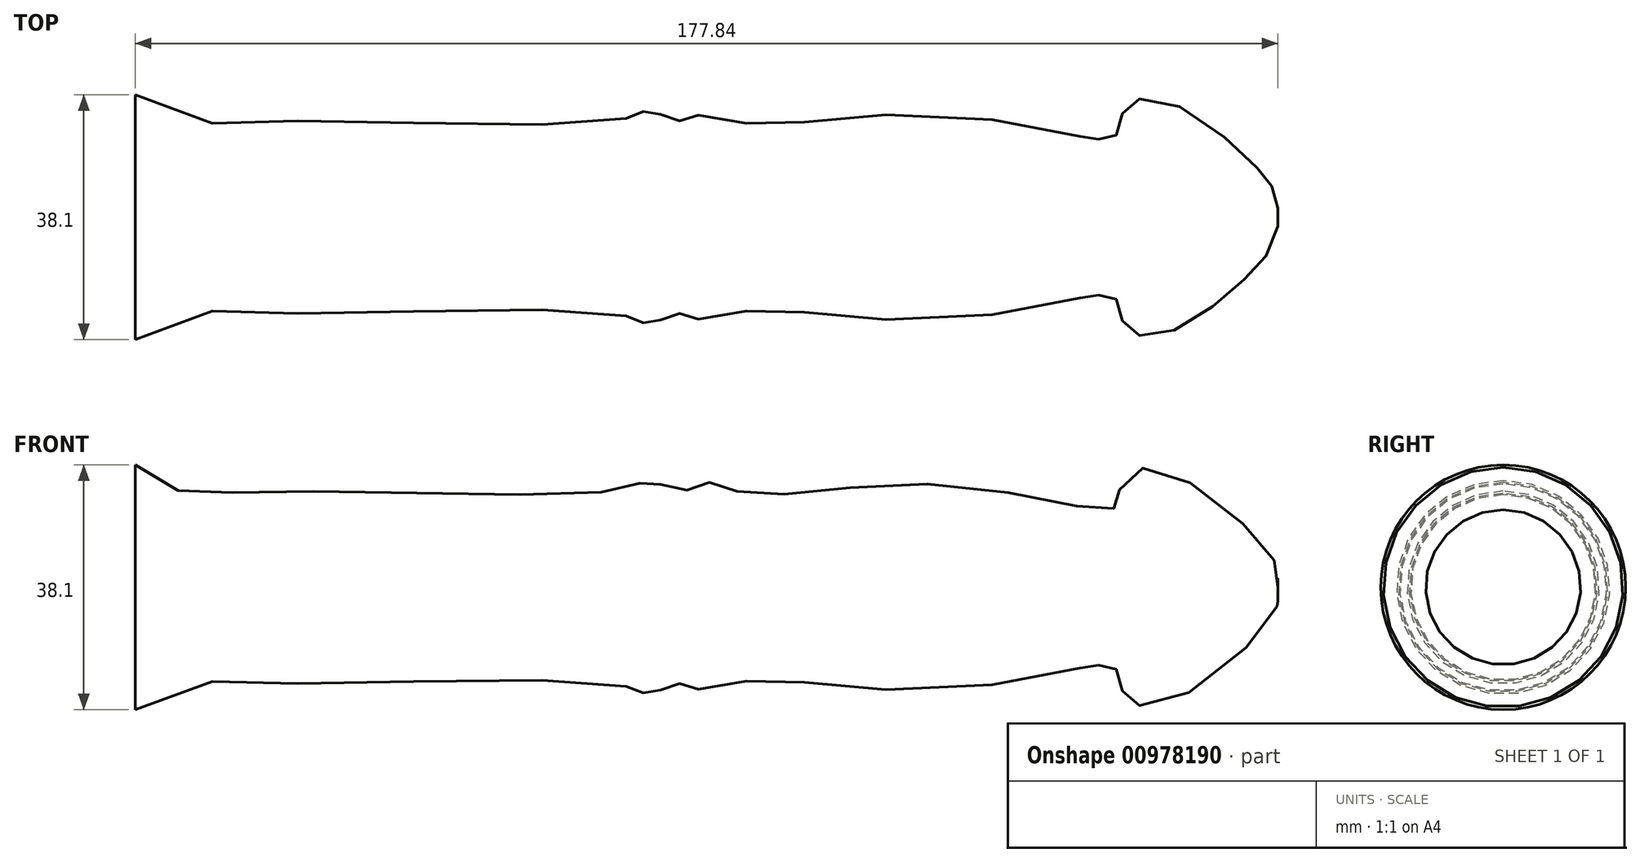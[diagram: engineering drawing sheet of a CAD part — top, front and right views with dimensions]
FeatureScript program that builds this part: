
annotation { "Feature Type Name" : "Feature", "Feature Type Description" : "" }
export const myFeature = defineFeature(function(context is Context, id is Id, definition is map)
    precondition{}
    {
        {
            var Q0;
            Q0=qCreatedBy(makeId("Front.planeOp"),FACE);
            var sketch = newSketch(context, id + "F0", { "sketchPlane" : qUnion([Q0])});
            skLineSegment(sketch, "E0.right", {"start": v(-88.9, 19.05) * mm, "end": v(-88.9, 0) * mm});
            skPoint(sketch, "E0.middle", {"position": v(0, 0) * mm});
            skLineSegment(sketch, "E1", {"start": v(-88.9, 0) * mm, "end": v(88.9, 0) * mm});
            skFitSpline(sketch, "E2", {"points": [v(-88.9, 19.05) * mm, v(-68.88, 14.9) * mm, v(-12.62, 15.36) * mm, v(-8.8, 16.59) * mm, v(-3.86, 14.96) * mm, v(0, 16.28) * mm, v(6.03, 14.62) * mm, v(37.07, 15.98) * mm, v(63.33, 12.23) * mm, v(64, 14.28) * mm, v(68.77, 18.66) * mm, v(87.5, 5.49) * mm, v(88.9, 0) * mm], "startDerivative": vector(153.99, -157.05) * mm, "endDerivative": vector(-4.41, -120.62) * mm});
            skSolve(sketch);
        }
        {
            var Q0;
            Q0=makeQuery(id+"F0.imprint","IMPRINT",FACE,{"disambiguationData":[TD([[makeQuery(id+"F0.imprint","IMPRINT",EDGE,{"derivedFrom":sQuery(id+"F0.wireOp",EDGE,"E0.right")}),1.0]])]});
            var Q1;
            Q1=sQuery(id+"F0.wireOp",EDGE,"E1");
            revolve(context, id + "F1", {"surfaceOperationType" : NewSurfaceOperationType.NEW, "entities" : qUnion([Q0]), "axis" : qUnion([Q1]), "revolveType" : RevolveType.FULL});
        }
    });
